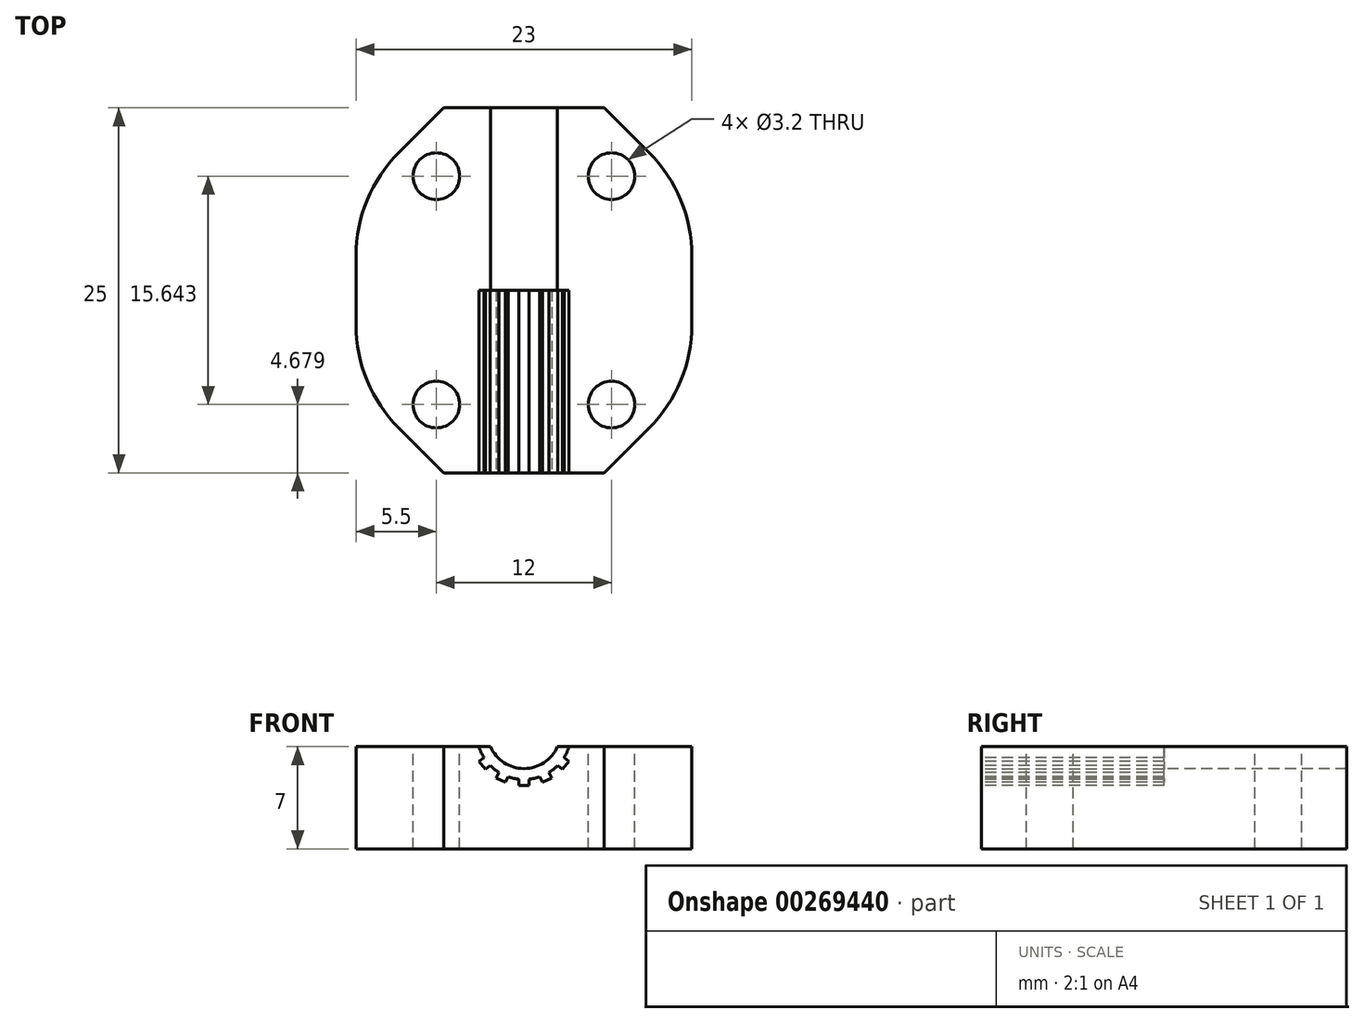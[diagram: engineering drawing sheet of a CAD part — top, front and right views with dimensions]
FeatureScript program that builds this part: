
annotation { "Feature Type Name" : "Feature", "Feature Type Description" : "" }
export const myFeature = defineFeature(function(context is Context, id is Id, definition is map)
    precondition{}
    {
        {
            var Q0;
            Q0=qCreatedBy(makeId("Top.planeOp"),FACE);
            var sketch = newSketch(context, id + "F0", { "sketchPlane" : qUnion([Q0])});
            skLineSegment(sketch, "E0.bottom", {"start": v(11.5, 12.5) * mm, "end": v(-11.5, 12.5) * mm});
            skLineSegment(sketch, "E0.top", {"start": v(11.5, -12.5) * mm, "end": v(-11.5, -12.5) * mm});
            skLineSegment(sketch, "E0.left", {"start": v(11.5, 12.5) * mm, "end": v(11.5, -12.5) * mm});
            skLineSegment(sketch, "E0.right", {"start": v(-11.5, 12.5) * mm, "end": v(-11.5, -12.5) * mm});
            skPoint(sketch, "E0.middle", {"position": v(0, 0) * mm});
            skLineSegment(sketch, "E1", {"start": v(11.5, -12.5) * mm, "end": v(-11.5, 12.5) * mm, "construction": true});
            skSolve(sketch);
        }
        {
            var Q0;
            Q0 = qSketchRegion(id + "F0", true);
            extrude(context, id + "F1", {"entities" : qUnion([Q0]), "depth" : 7 * mm});
        }
        {
            var Q0;
            Q0=makeQuery(id+"F1.opExtrude","SWEPT_FACE",FACE,{"disambiguationData":[OSD([sQuery(id+"F0.wireOp",EDGE,"E0.top")])]});
            var sketch = newSketch(context, id + "F2", { "sketchPlane" : qUnion([Q0])});
            skCircle(sketch, "E2", {"center": v(0, 8) * mm, "radius": 2.5 * mm});
            skPoint(sketch, "E2.centerSnap0", {"position": v(0, 7) * mm});
            skLineSegment(sketch, "E3", {"start": v(0, 7) * mm, "end": v(0, 8) * mm});
            skCircle(sketch, "E4", {"center": v(0, 8) * mm, "radius": 3.25 * mm});
            skLineSegment(sketch, "E5", {"start": v(0, 7) * mm, "end": v(0, 5.02) * mm, "construction": true});
            skLineSegment(sketch, "E6.bottom", {"start": v(0.35, 4.35) * mm, "end": v(-0.35, 4.35) * mm});
            skLineSegment(sketch, "E6.top", {"start": v(0.35, 5.15) * mm, "end": v(-0.35, 5.15) * mm});
            skLineSegment(sketch, "E6.left", {"start": v(0.35, 4.35) * mm, "end": v(0.35, 5.15) * mm});
            skLineSegment(sketch, "E6.right", {"start": v(-0.35, 4.35) * mm, "end": v(-0.35, 5.15) * mm});
            skPoint(sketch, "E6.middle", {"position": v(0, 4.75) * mm});
            skLineSegment(sketch, "E7.1.0", {"start": v(-1.27, 4.56) * mm, "end": v(-0.92, 5.28) * mm});
            skLineSegment(sketch, "E7.1.1", {"start": v(-0.92, 5.28) * mm, "end": v(-1.55, 5.58) * mm});
            skLineSegment(sketch, "E7.1.2", {"start": v(-1.9, 4.86) * mm, "end": v(-1.55, 5.58) * mm});
            skLineSegment(sketch, "E7.1.3", {"start": v(-1.27, 4.56) * mm, "end": v(-1.9, 4.86) * mm});
            skLineSegment(sketch, "E7.2.0", {"start": v(-2.64, 5.45) * mm, "end": v(-2, 5.95) * mm});
            skLineSegment(sketch, "E7.2.1", {"start": v(-2, 5.95) * mm, "end": v(-2.45, 6.5) * mm});
            skLineSegment(sketch, "E7.2.2", {"start": v(-3.07, 6) * mm, "end": v(-2.45, 6.5) * mm});
            skLineSegment(sketch, "E7.2.3", {"start": v(-2.64, 5.45) * mm, "end": v(-3.07, 6) * mm});
            skLineSegment(sketch, "E7.3.0", {"start": v(-3.48, 6.85) * mm, "end": v(-2.7, 7.02) * mm});
            skLineSegment(sketch, "E7.3.1", {"start": v(-2.7, 7.02) * mm, "end": v(-2.86, 7.7) * mm});
            skLineSegment(sketch, "E7.3.2", {"start": v(-3.64, 7.53) * mm, "end": v(-2.86, 7.7) * mm});
            skLineSegment(sketch, "E7.3.3", {"start": v(-3.48, 6.85) * mm, "end": v(-3.64, 7.53) * mm});
            skLineSegment(sketch, "E7.4.0", {"start": v(-3.64, 8.47) * mm, "end": v(-2.86, 8.3) * mm});
            skLineSegment(sketch, "E7.4.1", {"start": v(-2.86, 8.3) * mm, "end": v(-2.7, 8.98) * mm});
            skLineSegment(sketch, "E7.4.2", {"start": v(-3.48, 9.15) * mm, "end": v(-2.7, 8.98) * mm});
            skLineSegment(sketch, "E7.4.3", {"start": v(-3.64, 8.47) * mm, "end": v(-3.48, 9.15) * mm});
            skLineSegment(sketch, "E7.5.0", {"start": v(-3.07, 10) * mm, "end": v(-2.45, 9.5) * mm});
            skLineSegment(sketch, "E7.5.1", {"start": v(-2.45, 9.5) * mm, "end": v(-2, 10.05) * mm});
            skLineSegment(sketch, "E7.5.2", {"start": v(-2.64, 10.55) * mm, "end": v(-2, 10.05) * mm});
            skLineSegment(sketch, "E7.5.3", {"start": v(-3.07, 10) * mm, "end": v(-2.64, 10.55) * mm});
            skLineSegment(sketch, "E7.6.0", {"start": v(-1.9, 11.14) * mm, "end": v(-1.55, 10.42) * mm});
            skLineSegment(sketch, "E7.6.1", {"start": v(-1.55, 10.42) * mm, "end": v(-0.92, 10.72) * mm});
            skLineSegment(sketch, "E7.6.2", {"start": v(-1.27, 11.44) * mm, "end": v(-0.92, 10.72) * mm});
            skLineSegment(sketch, "E7.6.3", {"start": v(-1.9, 11.14) * mm, "end": v(-1.27, 11.44) * mm});
            skLineSegment(sketch, "E7.7.0", {"start": v(-0.35, 11.65) * mm, "end": v(-0.35, 10.85) * mm});
            skLineSegment(sketch, "E7.7.1", {"start": v(-0.35, 10.85) * mm, "end": v(0.35, 10.85) * mm});
            skLineSegment(sketch, "E7.7.2", {"start": v(0.35, 11.65) * mm, "end": v(0.35, 10.85) * mm});
            skLineSegment(sketch, "E7.7.3", {"start": v(-0.35, 11.65) * mm, "end": v(0.35, 11.65) * mm});
            skLineSegment(sketch, "E7.8.0", {"start": v(1.27, 11.44) * mm, "end": v(0.92, 10.72) * mm});
            skLineSegment(sketch, "E7.8.1", {"start": v(0.92, 10.72) * mm, "end": v(1.55, 10.42) * mm});
            skLineSegment(sketch, "E7.8.2", {"start": v(1.9, 11.14) * mm, "end": v(1.55, 10.42) * mm});
            skLineSegment(sketch, "E7.8.3", {"start": v(1.27, 11.44) * mm, "end": v(1.9, 11.14) * mm});
            skLineSegment(sketch, "E7.9.0", {"start": v(2.64, 10.55) * mm, "end": v(2, 10.05) * mm});
            skLineSegment(sketch, "E7.9.1", {"start": v(2, 10.05) * mm, "end": v(2.45, 9.5) * mm});
            skLineSegment(sketch, "E7.9.2", {"start": v(3.07, 10) * mm, "end": v(2.45, 9.5) * mm});
            skLineSegment(sketch, "E7.9.3", {"start": v(2.64, 10.55) * mm, "end": v(3.07, 10) * mm});
            skLineSegment(sketch, "E7.10.0", {"start": v(3.48, 9.15) * mm, "end": v(2.7, 8.98) * mm});
            skLineSegment(sketch, "E7.10.1", {"start": v(2.7, 8.98) * mm, "end": v(2.86, 8.3) * mm});
            skLineSegment(sketch, "E7.10.2", {"start": v(3.64, 8.47) * mm, "end": v(2.86, 8.3) * mm});
            skLineSegment(sketch, "E7.10.3", {"start": v(3.48, 9.15) * mm, "end": v(3.64, 8.47) * mm});
            skLineSegment(sketch, "E7.11.0", {"start": v(3.64, 7.53) * mm, "end": v(2.86, 7.7) * mm});
            skLineSegment(sketch, "E7.11.1", {"start": v(2.86, 7.7) * mm, "end": v(2.7, 7.02) * mm});
            skLineSegment(sketch, "E7.11.2", {"start": v(3.48, 6.85) * mm, "end": v(2.7, 7.02) * mm});
            skLineSegment(sketch, "E7.11.3", {"start": v(3.64, 7.53) * mm, "end": v(3.48, 6.85) * mm});
            skLineSegment(sketch, "E7.12.0", {"start": v(3.07, 6) * mm, "end": v(2.45, 6.5) * mm});
            skLineSegment(sketch, "E7.12.1", {"start": v(2.45, 6.5) * mm, "end": v(2, 5.95) * mm});
            skLineSegment(sketch, "E7.12.2", {"start": v(2.64, 5.45) * mm, "end": v(2, 5.95) * mm});
            skLineSegment(sketch, "E7.12.3", {"start": v(3.07, 6) * mm, "end": v(2.64, 5.45) * mm});
            skLineSegment(sketch, "E7.13.0", {"start": v(1.9, 4.86) * mm, "end": v(1.55, 5.58) * mm});
            skLineSegment(sketch, "E7.13.1", {"start": v(1.55, 5.58) * mm, "end": v(0.92, 5.28) * mm});
            skLineSegment(sketch, "E7.13.2", {"start": v(1.27, 4.56) * mm, "end": v(0.92, 5.28) * mm});
            skLineSegment(sketch, "E7.13.3", {"start": v(1.9, 4.86) * mm, "end": v(1.27, 4.56) * mm});
            skLineSegment(sketch, "E7.anchor1", {"start": v(0, 8) * mm, "end": v(0.35, 5.15) * mm, "construction": true});
            skLineSegment(sketch, "E7.anchor2", {"start": v(0, 8) * mm, "end": v(0.35, 5.15) * mm, "construction": true});
            skSolve(sketch);
        }
        {
            var Q0;
            {var subQ1=makeQuery(id+"F1.opExtrude","CAP_EDGE",EDGE,{"disambiguationData":[OSD([sQuery(id+"F0.wireOp",EDGE,"E0.top")])],"isStart":false});var subQ4=makeQuery(id+"F2.imprint","IMPRINT",VERTEX,{"derivedFrom":subQ1});Q0=makeQuery(id+"F2.imprint","IMPRINT",FACE,{"disambiguationData":[TD([[makeQuery(id+"F2.imprint","IMPRINT",EDGE,{"disambiguationData":[TD([[subQ4,1.0]])],"derivedFrom":subQ1}),1.0]])]});}
            extrude(context, id + "F3", {"entities" : qUnion([Q0]), "operationType" : NewBodyOperationType.REMOVE, "endBound" : BoundingType.THROUGH_ALL, "oppositeDirection" : true, "depth" : 25 * mm});
        }
        {
            var Q0;
            {var subQ0=sQuery(id+"F2.wireOp",EDGE,"E2");var subQ1=makeQuery(id+"F1.opExtrude","CAP_EDGE",EDGE,{"disambiguationData":[OSD([sQuery(id+"F0.wireOp",EDGE,"E0.top")])],"isStart":false});var subQ2=makeQuery(id+"F2.imprint","INTERSECT",VERTEX,{"disambiguationData":[OD(0.0)],"derivedFrom":[subQ1,subQ0]});Q0=makeQuery(id+"F2.imprint","IMPRINT",FACE,{"disambiguationData":[TD([[makeQuery(id+"F2.imprint","IMPRINT",EDGE,{"disambiguationData":[TD([[subQ2,-1.0]])],"derivedFrom":subQ0}),-1.0]])]});}
            var Q1;
            Q1=makeQuery(id+"F2.imprint","IMPRINT",FACE,{"disambiguationData":[TD([[makeQuery(id+"F2.imprint","IMPRINT",EDGE,{"derivedFrom":sQuery(id+"F2.wireOp",EDGE,"E7.12.0")}),1.0]])]});
            var Q2;
            Q2=makeQuery(id+"F2.imprint","IMPRINT",FACE,{"disambiguationData":[TD([[makeQuery(id+"F2.imprint","IMPRINT",EDGE,{"derivedFrom":sQuery(id+"F2.wireOp",EDGE,"E7.13.0")}),1.0]])]});
            var Q3;
            Q3=makeQuery(id+"F2.imprint","IMPRINT",FACE,{"disambiguationData":[TD([[makeQuery(id+"F2.imprint","IMPRINT",EDGE,{"derivedFrom":sQuery(id+"F2.wireOp",EDGE,"E6.left")}),1.0]])]});
            var Q4;
            Q4=makeQuery(id+"F2.imprint","IMPRINT",FACE,{"disambiguationData":[TD([[makeQuery(id+"F2.imprint","IMPRINT",EDGE,{"derivedFrom":sQuery(id+"F2.wireOp",EDGE,"E7.1.0")}),1.0]])]});
            var Q5;
            Q5=makeQuery(id+"F2.imprint","IMPRINT",FACE,{"disambiguationData":[TD([[makeQuery(id+"F2.imprint","IMPRINT",EDGE,{"derivedFrom":sQuery(id+"F2.wireOp",EDGE,"E7.2.0")}),1.0]])]});
            var Q6;
            {var subQ0=sQuery(id+"F2.wireOp",EDGE,"E7.11.2");var subQ1=sQuery(id+"F2.wireOp",EDGE,"E4");var subQ2=makeQuery(id+"F2.imprint","INTERSECT",VERTEX,{"derivedFrom":[subQ1,subQ0]});Q6=makeQuery(id+"F2.imprint","IMPRINT",FACE,{"disambiguationData":[TD([[makeQuery(id+"F2.imprint","IMPRINT",EDGE,{"disambiguationData":[TD([[subQ2,-1.0]])],"derivedFrom":subQ1}),1.0]])]});}
            var Q7;
            {var subQ0=sQuery(id+"F2.wireOp",EDGE,"E7.3.0");var subQ1=sQuery(id+"F2.wireOp",EDGE,"E4");var subQ2=makeQuery(id+"F2.imprint","INTERSECT",VERTEX,{"derivedFrom":[subQ1,subQ0]});Q7=makeQuery(id+"F2.imprint","IMPRINT",FACE,{"disambiguationData":[TD([[makeQuery(id+"F2.imprint","IMPRINT",EDGE,{"disambiguationData":[TD([[subQ2,1.0]])],"derivedFrom":subQ1}),1.0]])]});}
            extrude(context, id + "F4", {"entities" : qUnion([Q0, Q1, Q2, Q3, Q4, Q5, Q6, Q7]), "operationType" : NewBodyOperationType.REMOVE, "oppositeDirection" : true, "depth" : 12.5 * mm});
        }
        {
            var Q0;
            Q0=makeQuery(id+"F1.opExtrude","SWEPT_EDGE",EDGE,{"disambiguationData":[OSD([sQuery(id+"F0.wireOp",EDGE,"E0.top"),sQuery(id+"F0.wireOp",EDGE,"E0.left")])]});
            var Q1;
            Q1=makeQuery(id+"F1.opExtrude","SWEPT_EDGE",EDGE,{"disambiguationData":[OSD([sQuery(id+"F0.wireOp",EDGE,"E0.top"),sQuery(id+"F0.wireOp",EDGE,"E0.right")])]});
            var Q2;
            Q2=makeQuery(id+"F1.opExtrude","SWEPT_EDGE",EDGE,{"disambiguationData":[OSD([sQuery(id+"F0.wireOp",EDGE,"E0.bottom"),sQuery(id+"F0.wireOp",EDGE,"E0.left")])]});
            var Q3;
            Q3=makeQuery(id+"F1.opExtrude","SWEPT_EDGE",EDGE,{"disambiguationData":[OSD([sQuery(id+"F0.wireOp",EDGE,"E0.bottom"),sQuery(id+"F0.wireOp",EDGE,"E0.right")])]});
            chamfer(context, id + "F5", {"entities" : qUnion([Q0, Q1, Q2, Q3]), "width" : 6 * mm, "tangentPropagation" : true});
        }
        {
            var Q0;
            {var subQ0=sQuery(id+"F0.wireOp",EDGE,"E0.left");Q0=makeQuery(id+"F5.opChamfer","BLEND_EDGE",EDGE,{"blendedFrom":[makeQuery(id+"F1.opExtrude","SWEPT_EDGE",EDGE,{"disambiguationData":[OSD([sQuery(id+"F0.wireOp",EDGE,"E0.bottom"),subQ0])]}),makeQuery(id+"F1.opExtrude","SWEPT_FACE",FACE,{"disambiguationData":[OSD([subQ0])]})],"blendedInto":[makeQuery(id+"F1.opExtrude","SWEPT_FACE",FACE,{"disambiguationData":[OSD([subQ0])]})]});}
            var Q1;
            {var subQ0=sQuery(id+"F0.wireOp",EDGE,"E0.left");Q1=makeQuery(id+"F5.opChamfer","BLEND_EDGE",EDGE,{"blendedFrom":[makeQuery(id+"F1.opExtrude","SWEPT_EDGE",EDGE,{"disambiguationData":[OSD([sQuery(id+"F0.wireOp",EDGE,"E0.top"),subQ0])]}),makeQuery(id+"F1.opExtrude","SWEPT_FACE",FACE,{"disambiguationData":[OSD([subQ0])]})],"blendedInto":[makeQuery(id+"F1.opExtrude","SWEPT_FACE",FACE,{"disambiguationData":[OSD([subQ0])]})]});}
            var Q2;
            {var subQ0=sQuery(id+"F0.wireOp",EDGE,"E0.right");Q2=makeQuery(id+"F5.opChamfer","BLEND_EDGE",EDGE,{"blendedFrom":[makeQuery(id+"F1.opExtrude","SWEPT_EDGE",EDGE,{"disambiguationData":[OSD([sQuery(id+"F0.wireOp",EDGE,"E0.bottom"),subQ0])]}),makeQuery(id+"F1.opExtrude","SWEPT_FACE",FACE,{"disambiguationData":[OSD([subQ0])]})],"blendedInto":[makeQuery(id+"F1.opExtrude","SWEPT_FACE",FACE,{"disambiguationData":[OSD([subQ0])]})]});}
            var Q3;
            {var subQ0=sQuery(id+"F0.wireOp",EDGE,"E0.right");Q3=makeQuery(id+"F5.opChamfer","BLEND_EDGE",EDGE,{"blendedFrom":[makeQuery(id+"F1.opExtrude","SWEPT_EDGE",EDGE,{"disambiguationData":[OSD([sQuery(id+"F0.wireOp",EDGE,"E0.top"),subQ0])]}),makeQuery(id+"F1.opExtrude","SWEPT_FACE",FACE,{"disambiguationData":[OSD([subQ0])]})],"blendedInto":[makeQuery(id+"F1.opExtrude","SWEPT_FACE",FACE,{"disambiguationData":[OSD([subQ0])]})]});}
            fillet(context, id + "F6", {"entities" : qUnion([Q0, Q1, Q2, Q3]), "radius" : 10 * mm, "tangentPropagation" : true, "allowEdgeOverflow" : false});
        }
        {
            var Q0;
            {var subQ0=sQuery(id+"F0.wireOp",EDGE,"E0.bottom");var subQ1=sQuery(id+"F0.wireOp",EDGE,"E0.top");var subQ2=sQuery(id+"F0.wireOp",EDGE,"E0.left");Q0=makeQuery(id+"F3.boolean.opBoolean","SPLIT",FACE,{"disambiguationData":[TD([makeQuery(id+"F1.opExtrude","SWEPT_FACE",FACE,{"disambiguationData":[OSD([subQ2])]})])],"derivedFrom":makeQuery(id+"F1.opExtrude","CAP_FACE",FACE,{"disambiguationData":[OSD([subQ0,subQ1,subQ2,sQuery(id+"F0.wireOp",EDGE,"E0.right")])],"isStart":false})});}
            var sketch = newSketch(context, id + "F7", { "sketchPlane" : qUnion([Q0])});
            skLineSegment(sketch, "E8.bottom", {"start": v(-6, -7.82) * mm, "end": v(6, -7.82) * mm, "construction": true});
            skLineSegment(sketch, "E8.top", {"start": v(-6, 7.82) * mm, "end": v(6, 7.82) * mm, "construction": true});
            skLineSegment(sketch, "E8.left", {"start": v(-6, -7.82) * mm, "end": v(-6, 7.82) * mm, "construction": true});
            skLineSegment(sketch, "E8.right", {"start": v(6, -7.82) * mm, "end": v(6, 7.82) * mm, "construction": true});
            skPoint(sketch, "E8.middle", {"position": v(0, 0) * mm});
            skCircle(sketch, "E9", {"center": v(6, -7.82) * mm, "radius": 1.6 * mm});
            skCircle(sketch, "E10", {"center": v(-6, -7.82) * mm, "radius": 1.6 * mm});
            skCircle(sketch, "E11", {"center": v(-6, 7.82) * mm, "radius": 1.6 * mm});
            skCircle(sketch, "E12", {"center": v(6, 7.82) * mm, "radius": 1.6 * mm});
            skSolve(sketch);
        }
        {
            var Q0;
            Q0 = qSketchRegion(id + "F7", true);
            extrude(context, id + "F8", {"entities" : qUnion([Q0]), "operationType" : NewBodyOperationType.REMOVE, "oppositeDirection" : true, "depth" : 25 * mm});
        }
    });
